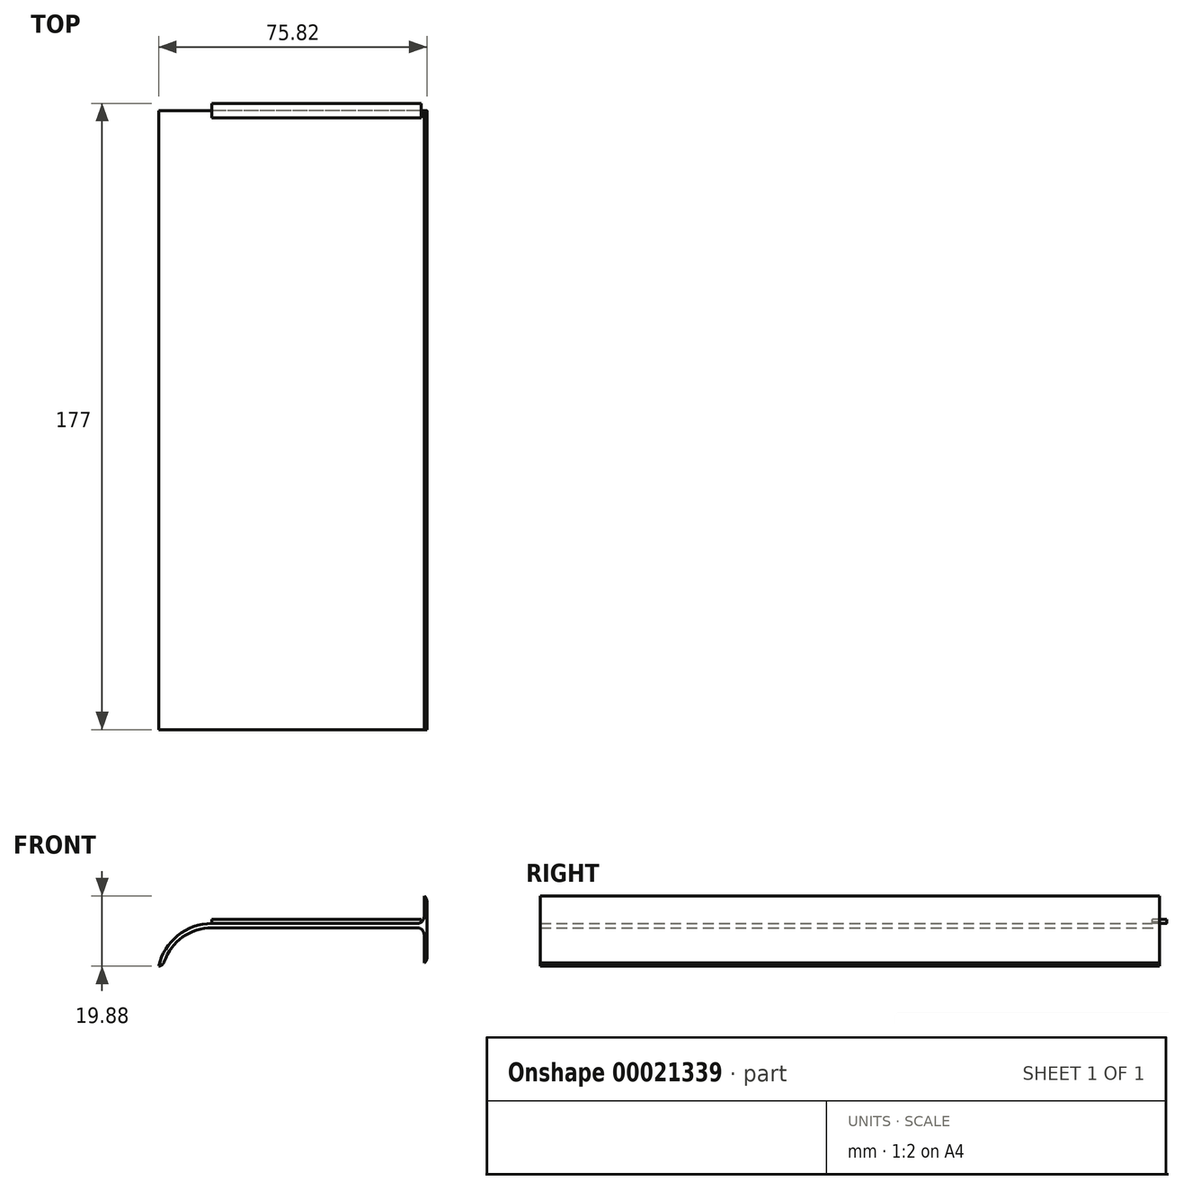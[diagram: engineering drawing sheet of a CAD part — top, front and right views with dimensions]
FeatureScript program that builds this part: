
annotation { "Feature Type Name" : "Feature", "Feature Type Description" : "" }
export const myFeature = defineFeature(function(context is Context, id is Id, definition is map)
    precondition{}
    {
        {
            var Q0;
            Q0=qCreatedBy(makeId("Front.planeOp"),FACE);
            var sketch = newSketch(context, id + "F0", { "sketchPlane" : qUnion([Q0])});
            skLineSegment(sketch, "E0.bottom", {"start": v(87.58, 0) * mm, "end": v(86.78, 0) * mm});
            skLineSegment(sketch, "E0.top", {"start": v(87.58, -19) * mm, "end": v(86.78, -19) * mm});
            skLineSegment(sketch, "E0.left", {"start": v(87.58, 0) * mm, "end": v(87.58, -19) * mm});
            skLineSegment(sketch, "E0.right", {"start": v(86.78, 0) * mm, "end": v(86.78, -19) * mm});
            skLineSegment(sketch, "E1", {"start": v(86.78, -19) * mm, "end": v(86.78, -9) * mm});
            skLineSegment(sketch, "E2.bottom", {"start": v(86.78, -9) * mm, "end": v(26.78, -9) * mm});
            skLineSegment(sketch, "E2.top", {"start": v(86.78, -7.8) * mm, "end": v(26.78, -7.8) * mm});
            skLineSegment(sketch, "E2.left", {"start": v(86.78, -9) * mm, "end": v(86.78, -7.8) * mm});
            skLineSegment(sketch, "E2.right", {"start": v(26.78, -9) * mm, "end": v(26.78, -7.8) * mm, "construction": true});
            skLineSegment(sketch, "E3", {"start": v(26.78, -9) * mm, "end": v(26.78, -19.88) * mm, "construction": true});
            skLineSegment(sketch, "E4", {"start": v(26.78, -19.88) * mm, "end": v(12.96, -19.88) * mm, "construction": true});
            skLineSegment(sketch, "E5", {"start": v(12.96, -19.88) * mm, "end": v(11.76, -19.88) * mm});
            skArc(sketch, "E6", {"start": v(26.78, -9) * mm, "mid": v(17.98, -12.05) * mm, "end": v(12.96, -19.88) * mm});
            skArc(sketch, "E7", {"start": v(26.78, -7.8) * mm, "mid": v(17.14, -11.2) * mm, "end": v(11.76, -19.88) * mm});
            skLineSegment(sketch, "E8", {"start": v(86.78, -9) * mm, "end": v(86.78, -7.8) * mm, "construction": true});
            skLineSegment(sketch, "E9.bottom", {"start": v(86.78, -7.8) * mm, "end": v(85.98, -7.8) * mm});
            skLineSegment(sketch, "E9.top", {"start": v(86.78, 0) * mm, "end": v(85.98, 0) * mm});
            skLineSegment(sketch, "E9.left", {"start": v(86.78, -7.8) * mm, "end": v(86.78, 0) * mm});
            skLineSegment(sketch, "E9.right", {"start": v(85.98, -7.8) * mm, "end": v(85.98, 0) * mm});
            skPoint(sketch, "E10.oppositeSnap0", {"position": v(85.98, -3.9) * mm});
            skLineSegment(sketch, "E10.bottom", {"start": v(86.78, -19) * mm, "end": v(85.98, -19) * mm});
            skLineSegment(sketch, "E10.top", {"start": v(86.78, -9) * mm, "end": v(85.98, -9) * mm});
            skLineSegment(sketch, "E10.right", {"start": v(85.98, -19) * mm, "end": v(85.98, -9) * mm});
            skLineSegment(sketch, "E11.bottom", {"start": v(85.98, -7.8) * mm, "end": v(26.78, -7.8) * mm});
            skLineSegment(sketch, "E11.top", {"start": v(85.98, -6.6) * mm, "end": v(26.78, -6.6) * mm});
            skLineSegment(sketch, "E11.left", {"start": v(85.98, -7.8) * mm, "end": v(85.98, -6.6) * mm});
            skLineSegment(sketch, "E11.right", {"start": v(26.78, -7.8) * mm, "end": v(26.78, -6.6) * mm});
            skSolve(sketch);
        }
        {
            var Q0;
            Q0=makeQuery(id+"F0.imprint","IMPRINT",FACE,{"disambiguationData":[TD([[makeQuery(id+"F0.imprint","IMPRINT",EDGE,{"derivedFrom":sQuery(id+"F0.wireOp",EDGE,"E5")}),-1.0]])]});
            var Q1;
            {var subQ3=sQuery(id+"F0.wireOp",EDGE,"E0.bottom");Q1=makeQuery(id+"F0.imprint","IMPRINT",FACE,{"disambiguationData":[TD([[makeQuery(id+"F0.imprint","IMPRINT",EDGE,{"derivedFrom":subQ3}),1.0]])]});}
            extrude(context, id + "F1", {"entities" : qUnion([Q0, Q1]), "depth" : 175 * mm, "offsetDistance" : 25 * mm});
        }
        {
            var Q0;
            {var subQ4=sQuery(id+"F0.wireOp",EDGE,"E11.top");Q0=makeQuery(id+"F0.imprint","IMPRINT",FACE,{"disambiguationData":[TD([[makeQuery(id+"F0.imprint","IMPRINT",EDGE,{"derivedFrom":subQ4}),1.0]])]});}
            extrude(context, id + "F2", {"entities" : qUnion([Q0]), "operationType" : NewBodyOperationType.ADD, "oppositeDirection" : true, "depth" : 2 * mm, "offsetDistance" : 25 * mm, "hasSecondDirection" : true, "secondDirectionOppositeDirection" : false, "secondDirectionDepth" : 2 * mm});
        }
        {
            var Q0;
            {var subQ0=sQuery(id+"F0.wireOp",EDGE,"E0.right");Q0=qUnion([makeQuery(id+"F1.opExtrude","SWEPT_EDGE",EDGE,{"disambiguationData":[OSD([subQ0,sQuery(id+"F0.wireOp",EDGE,"E2.bottom")])]}),makeQuery(id+"F1.opExtrude","SWEPT_EDGE",EDGE,{"disambiguationData":[OSD([subQ0,sQuery(id+"F0.wireOp",EDGE,"E2.top")])]})]);}
            var Q1;
            Q1=makeQuery(id+"F1.opExtrude","SWEPT_EDGE",EDGE,{"disambiguationData":[OSD([sQuery(id+"F0.wireOp",EDGE,"E2.bottom"),sQuery(id+"F0.wireOp",EDGE,"E6")])]});
            var Q2;
            Q2=makeQuery(id+"F1.opExtrude","SWEPT_EDGE",EDGE,{"disambiguationData":[OSD([sQuery(id+"F0.wireOp",EDGE,"E0.bottom"),sQuery(id+"F0.wireOp",EDGE,"E0.left")])]});
            var Q3;
            Q3=makeQuery(id+"F1.opExtrude","SWEPT_EDGE",EDGE,{"disambiguationData":[OSD([sQuery(id+"F0.wireOp",EDGE,"E5"),sQuery(id+"F0.wireOp",EDGE,"E6")])]});
            var Q4;
            Q4=makeQuery(id+"F1.opExtrude","SWEPT_EDGE",EDGE,{"disambiguationData":[OSD([sQuery(id+"F0.wireOp",EDGE,"E0.top"),sQuery(id+"F0.wireOp",EDGE,"E0.left")])]});
            fillet(context, id + "F3", {"entities" : qUnion([Q0, Q1, Q2, Q3, Q4]), "radius" : 2 * mm, "tangentPropagation" : true, "allowEdgeOverflow" : false});
        }
        {
            var Q0;
            Q0=makeQuery(id+"F2.opExtrude","CAP_EDGE",EDGE,{"disambiguationData":[OSD([sQuery(id+"F0.wireOp",EDGE,"E2.top")])],"isStart":true});
            var Q1;
            Q1=makeQuery(id+"F2.opExtrude","CAP_EDGE",EDGE,{"disambiguationData":[OSD([sQuery(id+"F0.wireOp",EDGE,"E2.top")])],"isStart":false});
            fillet(context, id + "F4", {"entities" : qUnion([Q0, Q1]), "radius" : 0.1 * mm, "tangentPropagation" : true, "allowEdgeOverflow" : false});
        }
    });
